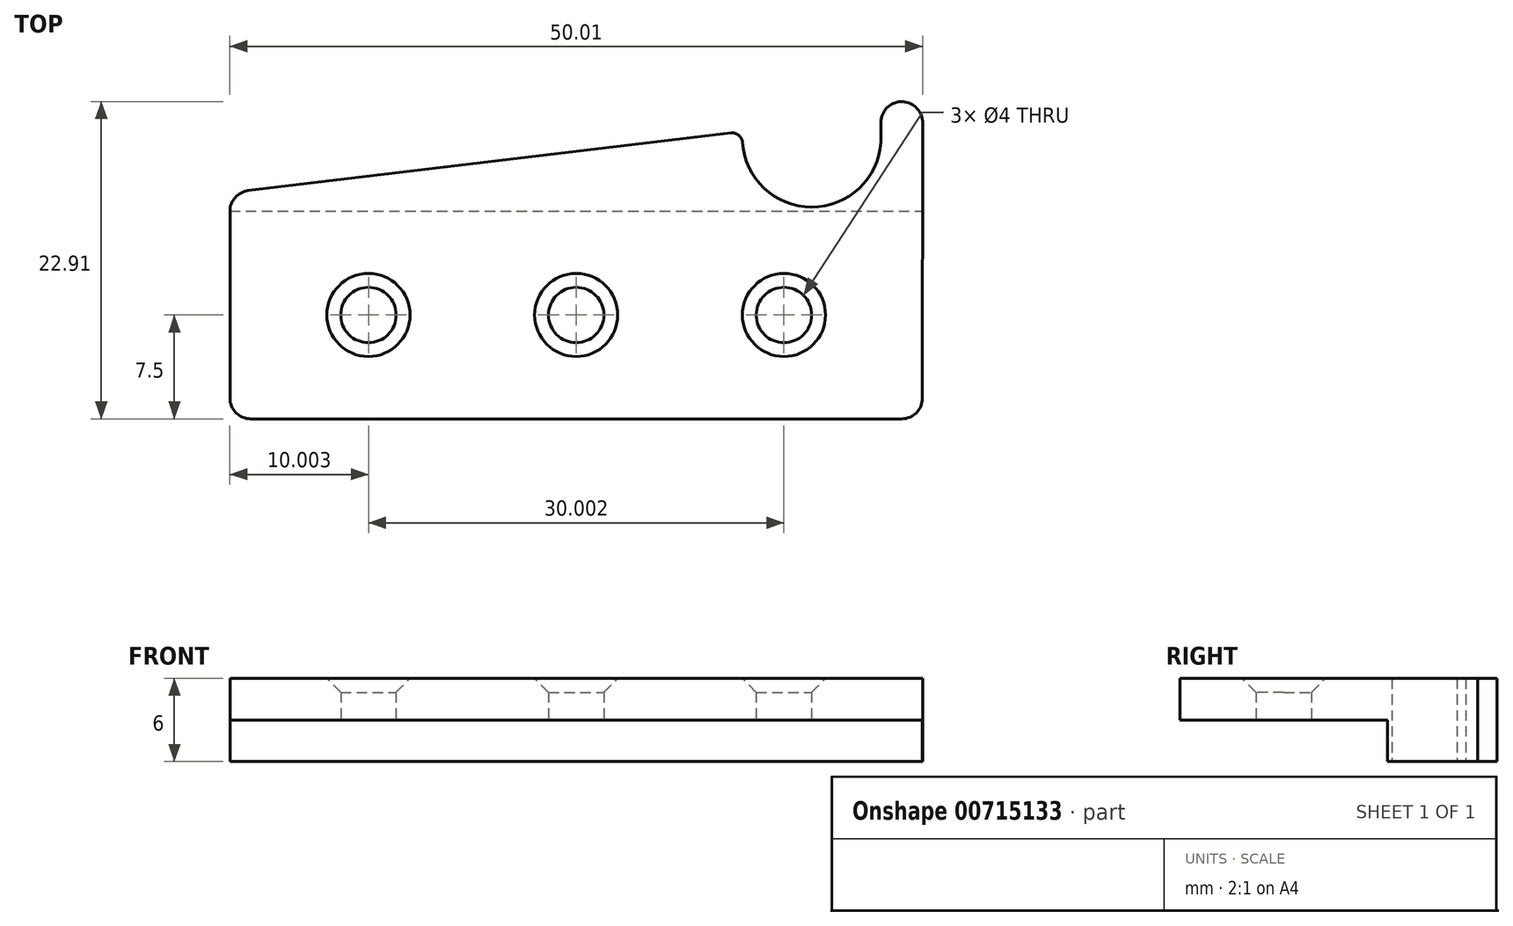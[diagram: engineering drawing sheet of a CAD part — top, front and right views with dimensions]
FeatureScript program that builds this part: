
annotation { "Feature Type Name" : "Feature", "Feature Type Description" : "" }
export const myFeature = defineFeature(function(context is Context, id is Id, definition is map)
    precondition{}
    {
        {
            var Q0;
            Q0=qCreatedBy(makeId("Top.planeOp"),FACE);
            var sketch = newSketch(context, id + "F0", { "sketchPlane" : qUnion([Q0])});
            skLineSegment(sketch, "E0", {"start": v(17.15, 13.15) * mm, "end": v(-17.7, 8.98) * mm});
            skPoint(sketch, "E1.visualSharp", {"position": v(30.99, 15.08) * mm});
            skArc(sketch, "E1.filletArc", {"start": v(30.99, 14) * mm, "mid": v(29.45, 15.4) * mm, "end": v(28, 13.9) * mm});
            skPoint(sketch, "E2.visualSharp", {"position": v(-19.02, 8.82) * mm});
            skArc(sketch, "E2.filletArc", {"start": v(-17.7, 8.98) * mm, "mid": v(-18.64, 8.5) * mm, "end": v(-19.02, 7.5) * mm});
            skCircle(sketch, "E3", {"center": v(-9.02, 0) * mm, "radius": 2 * mm});
            skCircle(sketch, "E4", {"center": v(5.98, 0) * mm, "radius": 2 * mm});
            skCircle(sketch, "E5", {"center": v(20.99, 0) * mm, "radius": 2 * mm});
            skLineSegment(sketch, "E6", {"start": v(-17.52, -7.5) * mm, "end": v(29.48, -7.5) * mm});
            skLineSegment(sketch, "E7", {"start": v(-19.02, 7.5) * mm, "end": v(-19.02, -6) * mm});
            skLineSegment(sketch, "E8", {"start": v(30.99, 14) * mm, "end": v(30.98, -6) * mm});
            skPoint(sketch, "E9.visualSharp", {"position": v(-19.02, -7.5) * mm});
            skArc(sketch, "E9.filletArc", {"start": v(-19.02, -6) * mm, "mid": v(-18.58, -7.06) * mm, "end": v(-17.52, -7.5) * mm});
            skPoint(sketch, "E10.visualSharp", {"position": v(30.98, -7.5) * mm});
            skArc(sketch, "E10.filletArc", {"start": v(29.48, -7.5) * mm, "mid": v(30.54, -7.06) * mm, "end": v(30.98, -6) * mm});
            skLineSegment(sketch, "E11.top", {"start": v(23, 7.8) * mm, "end": v(22.98, 7.8) * mm});
            skPoint(sketch, "E11.middle", {"position": v(23, 12.5) * mm});
            skPoint(sketch, "E12.visualSharp", {"position": v(28, 7.8) * mm});
            skArc(sketch, "E12.filletArc", {"start": v(23, 7.8) * mm, "mid": v(26.43, 9.16) * mm, "end": v(28, 12.5) * mm});
            skPoint(sketch, "E13.visualSharp", {"position": v(18, 7.8) * mm});
            skArc(sketch, "E13.filletArc", {"start": v(18, 12.5) * mm, "mid": v(19.55, 9.16) * mm, "end": v(22.98, 7.8) * mm});
            skLineSegment(sketch, "E14", {"start": v(28, 12.5) * mm, "end": v(28, 13.9) * mm});
            skArc(sketch, "E15", {"start": v(18, 12.5) * mm, "mid": v(17.7, 13) * mm, "end": v(17.15, 13.15) * mm});
            skSolve(sketch);
        }
        {
            var Q0;
            Q0=makeQuery(id+"F0.imprint","IMPRINT",FACE,{"disambiguationData":[TD([[makeQuery(id+"F0.imprint","IMPRINT",EDGE,{"derivedFrom":sQuery(id+"F0.wireOp",EDGE,"E0")}),1.0]])]});
            extrude(context, id + "F1", {"entities" : qUnion([Q0]), "depth" : 6 * mm, "offsetDistance" : 25 * mm});
        }
        {
            var Q0;
            Q0=makeQuery(id+"F1.opExtrude","CAP_FACE",FACE,{"disambiguationData":[OSD([sQuery(id+"F0.wireOp",EDGE,"E0"),sQuery(id+"F0.wireOp",EDGE,"E1.filletArc"),sQuery(id+"F0.wireOp",EDGE,"E2.filletArc"),sQuery(id+"F0.wireOp",EDGE,"E3"),sQuery(id+"F0.wireOp",EDGE,"E4"),sQuery(id+"F0.wireOp",EDGE,"E5"),sQuery(id+"F0.wireOp",EDGE,"E6"),sQuery(id+"F0.wireOp",EDGE,"E7"),sQuery(id+"F0.wireOp",EDGE,"E8"),sQuery(id+"F0.wireOp",EDGE,"E9.filletArc"),sQuery(id+"F0.wireOp",EDGE,"E10.filletArc"),sQuery(id+"F0.wireOp",EDGE,"E11.top"),sQuery(id+"F0.wireOp",EDGE,"E12.filletArc"),sQuery(id+"F0.wireOp",EDGE,"E13.filletArc"),sQuery(id+"F0.wireOp",EDGE,"E14"),sQuery(id+"F0.wireOp",EDGE,"E15")])],"isStart":true});
            var sketch = newSketch(context, id + "F2", { "sketchPlane" : qUnion([Q0])});
            skLineSegment(sketch, "E16.bottom", {"start": v(-19.02, -7.5) * mm, "end": v(30.98, -7.5) * mm});
            skLineSegment(sketch, "E16.top", {"start": v(-19.02, 7.5) * mm, "end": v(30.98, 7.5) * mm});
            skLineSegment(sketch, "E16.left", {"start": v(-19.02, -7.5) * mm, "end": v(-19.02, 7.5) * mm});
            skLineSegment(sketch, "E16.right", {"start": v(30.98, -7.5) * mm, "end": v(30.98, 7.5) * mm});
            skSolve(sketch);
        }
        {
            var Q0;
            Q0 = qSketchRegion(id + "F2", true);
            extrude(context, id + "F3", {"entities" : qUnion([Q0]), "operationType" : NewBodyOperationType.REMOVE, "oppositeDirection" : true, "depth" : 3 * mm, "offsetDistance" : 25 * mm});
        }
        {
            var Q0;
            Q0=makeQuery(id+"F1.opExtrude","CAP_EDGE",EDGE,{"disambiguationData":[OSD([sQuery(id+"F0.wireOp",EDGE,"E3")])],"isStart":false});
            chamfer(context, id + "F4", {"entities" : qUnion([Q0]), "width" : 1 * mm, "tangentPropagation" : true});
        }
        {
            var Q0;
            Q0=makeQuery(id+"F1.opExtrude","CAP_EDGE",EDGE,{"disambiguationData":[OSD([sQuery(id+"F0.wireOp",EDGE,"E4")])],"isStart":false});
            var Q1;
            Q1=makeQuery(id+"F1.opExtrude","CAP_EDGE",EDGE,{"disambiguationData":[OSD([sQuery(id+"F0.wireOp",EDGE,"E5")])],"isStart":false});
            chamfer(context, id + "F5", {"entities" : qUnion([Q0, Q1]), "width" : 1 * mm, "tangentPropagation" : true});
        }
    });
